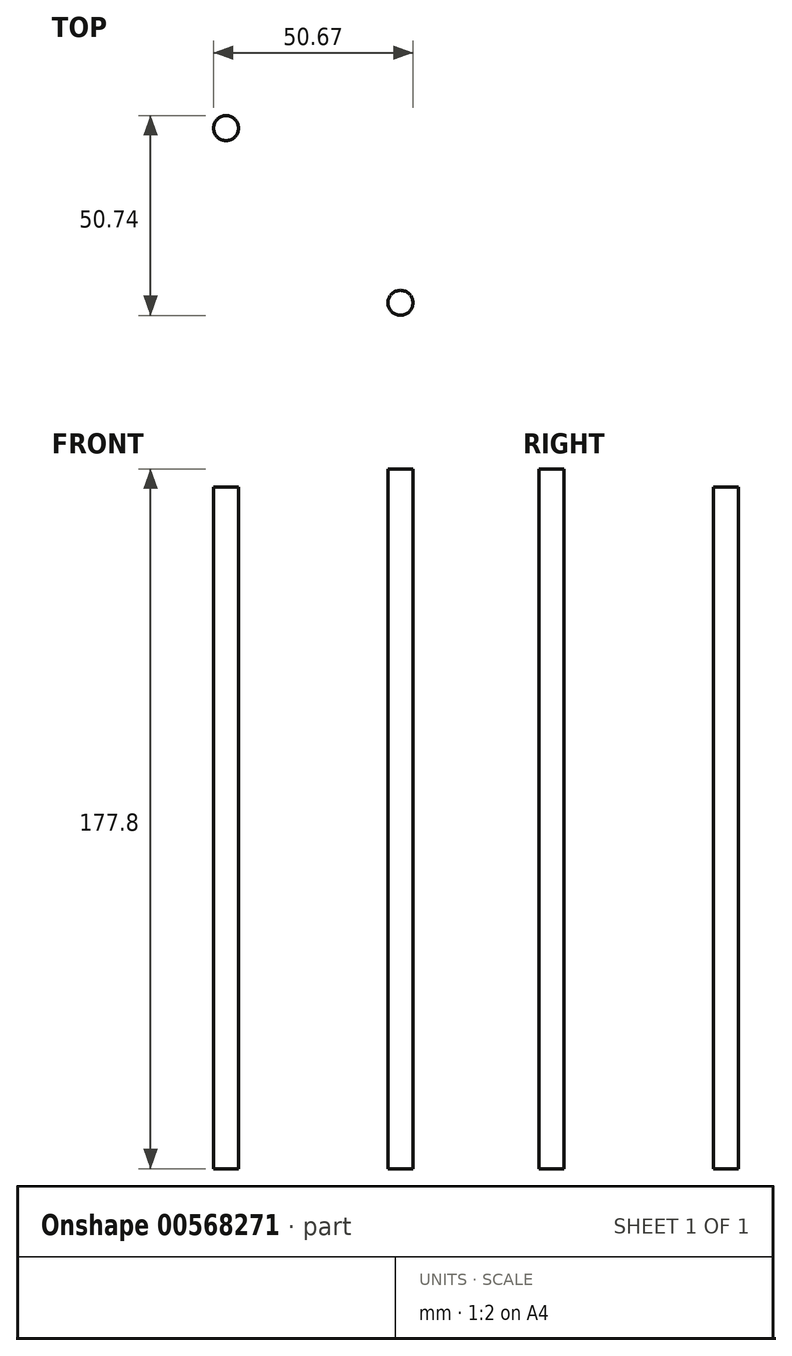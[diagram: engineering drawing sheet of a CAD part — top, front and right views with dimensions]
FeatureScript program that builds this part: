
annotation { "Feature Type Name" : "Feature", "Feature Type Description" : "" }
export const myFeature = defineFeature(function(context is Context, id is Id, definition is map)
    precondition{}
    {
        {
            var Q0;
            Q0=qCreatedBy(makeId("Top.planeOp"),FACE);
            var sketch = newSketch(context, id + "F0", { "sketchPlane" : qUnion([Q0])});
            skCircle(sketch, "E0", {"center": v(0.13, 0) * mm, "radius": 3.18 * mm});
            skSolve(sketch);
        }
        {
            var Q0;
            Q0 = qSketchRegion(id + "F0", true);
            extrude(context, id + "F1", {"entities" : qUnion([Q0]), "depth" : 177.8 * mm, "offsetDistance" : 25 * mm});
        }
        {
            var Q0;
            Q0=qCreatedBy(makeId("Top.planeOp"),FACE);
            var sketch = newSketch(context, id + "F2", { "sketchPlane" : qUnion([Q0])});
            skCircle(sketch, "E1", {"center": v(-44.18, 44.39) * mm, "radius": 3.18 * mm});
            skSolve(sketch);
        }
        {
            var Q0;
            Q0 = qSketchRegion(id + "F2", true);
            extrude(context, id + "F3", {"entities" : qUnion([Q0]), "depth" : 173.2 * mm, "offsetDistance" : 25 * mm});
        }
    });
